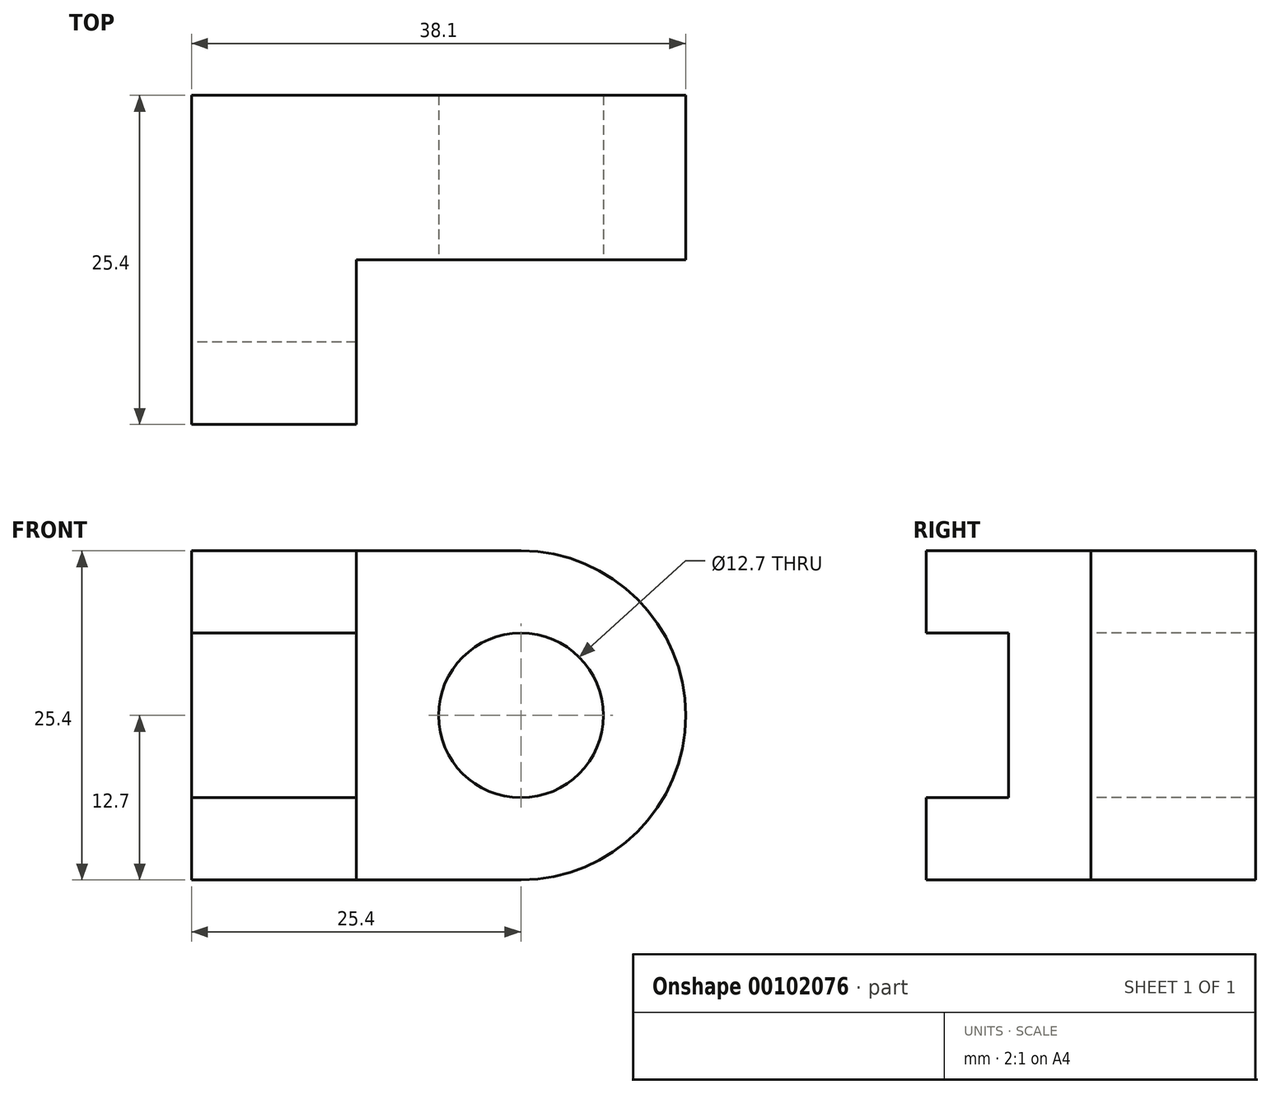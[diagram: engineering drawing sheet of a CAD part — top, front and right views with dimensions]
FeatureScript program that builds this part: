
annotation { "Feature Type Name" : "Feature", "Feature Type Description" : "" }
export const myFeature = defineFeature(function(context is Context, id is Id, definition is map)
    precondition{}
    {
        {
            var Q0;
            Q0=qCreatedBy(makeId("Top.planeOp"),FACE);
            var sketch = newSketch(context, id + "F0", { "sketchPlane" : qUnion([Q0])});
            skLineSegment(sketch, "E0", {"start": v(0, 0) * mm, "end": v(0, 25.4) * mm});
            skLineSegment(sketch, "E1", {"start": v(0, 25.4) * mm, "end": v(25.4, 25.4) * mm});
            skLineSegment(sketch, "E2", {"start": v(25.4, 25.4) * mm, "end": v(25.4, 12.7) * mm});
            skLineSegment(sketch, "E3", {"start": v(25.4, 12.7) * mm, "end": v(12.7, 12.7) * mm});
            skLineSegment(sketch, "E4", {"start": v(12.7, 12.7) * mm, "end": v(12.7, 0) * mm});
            skLineSegment(sketch, "E5", {"start": v(12.7, 0) * mm, "end": v(0, 0) * mm});
            skSolve(sketch);
        }
        {
            var Q0;
            Q0=makeQuery(id+"F0.imprint","IMPRINT",FACE,{"disambiguationData":[TD([[makeQuery(id+"F0.imprint","IMPRINT",EDGE,{"derivedFrom":sQuery(id+"F0.wireOp",EDGE,"E0")}),-1.0]])]});
            extrude(context, id + "F1", {"entities" : qUnion([Q0]), "oppositeDirection" : true, "depth" : 25.4 * mm});
        }
        {
            var Q0;
            Q0=makeQuery(id+"F1.opExtrude","SWEPT_FACE",FACE,{"disambiguationData":[OSD([sQuery(id+"F0.wireOp",EDGE,"E1")])]});
            var sketch = newSketch(context, id + "F2", { "sketchPlane" : qUnion([Q0])});
            skArc(sketch, "E6", {"start": v(-25.4, 0) * mm, "mid": v(-38.1, -12.7) * mm, "end": v(-25.4, -25.4) * mm});
            skSolve(sketch);
        }
        {
            var Q0;
            Q0=makeQuery(id+"F2.imprint","IMPRINT",FACE,{"disambiguationData":[TD([[makeQuery(id+"F2.imprint","IMPRINT",EDGE,{"derivedFrom":sQuery(id+"F2.wireOp",EDGE,"E6")}),1.0]])]});
            extrude(context, id + "F3", {"entities" : qUnion([Q0]), "operationType" : NewBodyOperationType.ADD, "oppositeDirection" : true, "depth" : 12.7 * mm});
        }
        {
            var Q0;
            Q0=makeQuery(id+"F1.opExtrude","SWEPT_FACE",FACE,{"disambiguationData":[OSD([sQuery(id+"F0.wireOp",EDGE,"E0")])]});
            var sketch = newSketch(context, id + "F4", { "sketchPlane" : qUnion([Q0])});
            skLineSegment(sketch, "E7.bottom", {"start": v(0, -6.35) * mm, "end": v(-6.35, -6.35) * mm});
            skLineSegment(sketch, "E7.top", {"start": v(0, -19.05) * mm, "end": v(-6.35, -19.05) * mm});
            skLineSegment(sketch, "E7.left", {"start": v(0, -6.35) * mm, "end": v(0, -19.05) * mm});
            skLineSegment(sketch, "E7.right", {"start": v(-6.35, -6.35) * mm, "end": v(-6.35, -19.05) * mm});
            skSolve(sketch);
        }
        {
            var Q0;
            Q0=makeQuery(id+"F4.imprint","IMPRINT",FACE,{"disambiguationData":[TD([[makeQuery(id+"F4.imprint","IMPRINT",EDGE,{"derivedFrom":sQuery(id+"F4.wireOp",EDGE,"E7.bottom")}),1.0]])]});
            extrude(context, id + "F5", {"entities" : qUnion([Q0]), "operationType" : NewBodyOperationType.REMOVE, "endBound" : BoundingType.THROUGH_ALL, "oppositeDirection" : true, "depth" : 25.4 * mm});
        }
        {
            var Q0;
            Q0=makeQuery(id+"F3.boolean.opBoolean","MERGE",FACE,{"derivedFrom":[makeQuery(id+"F1.opExtrude","SWEPT_FACE",FACE,{"disambiguationData":[OSD([sQuery(id+"F0.wireOp",EDGE,"E3")])]}),makeQuery(id+"F3.opExtrude","CAP_FACE",FACE,{"disambiguationData":[OSD([sQuery(id+"F0.wireOp",EDGE,"E1"),sQuery(id+"F0.wireOp",EDGE,"E2"),sQuery(id+"F2.wireOp",EDGE,"E6")])],"isStart":false})]});
            var sketch = newSketch(context, id + "F6", { "sketchPlane" : qUnion([Q0])});
            skCircle(sketch, "E8", {"center": v(25.4, -12.7) * mm, "radius": 6.35 * mm});
            skSolve(sketch);
        }
        {
            var Q0;
            Q0 = qSketchRegion(id + "F6", true);
            extrude(context, id + "F7", {"entities" : qUnion([Q0]), "operationType" : NewBodyOperationType.REMOVE, "endBound" : BoundingType.THROUGH_ALL, "oppositeDirection" : true, "depth" : 25.4 * mm});
        }
    });
